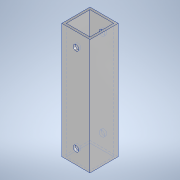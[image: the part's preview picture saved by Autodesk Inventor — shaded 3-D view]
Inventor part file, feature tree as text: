
AUTODESK INVENTOR PART (.ipt)
format: ipt  version: 2020.3 (Build 243373000, 373)  size: 116,224 bytes
history: native  units: mm
features: sketch x2, other x1, extrude x1, hole x1
ambient origin geometry x8: Origin, YZ Plane, XZ Plane, XY Plane, X Axis, Y Axis, Z Axis, Center Point
bodies: Body1 (feature_tree)
feature tree (5):
  other  "ソリッド1"
  extrude  "押し出し1"  Depth=15.0mm
  hole  "穴1"  [1 undecoded]
  sketch  "スケッチ1"
  sketch  "スケッチ2"
note: 1 required parameter value undecoded (feature->parameter linkage not recoverable at this tier; creation-order binding heuristic only, values carry confidence <= 0.55)
